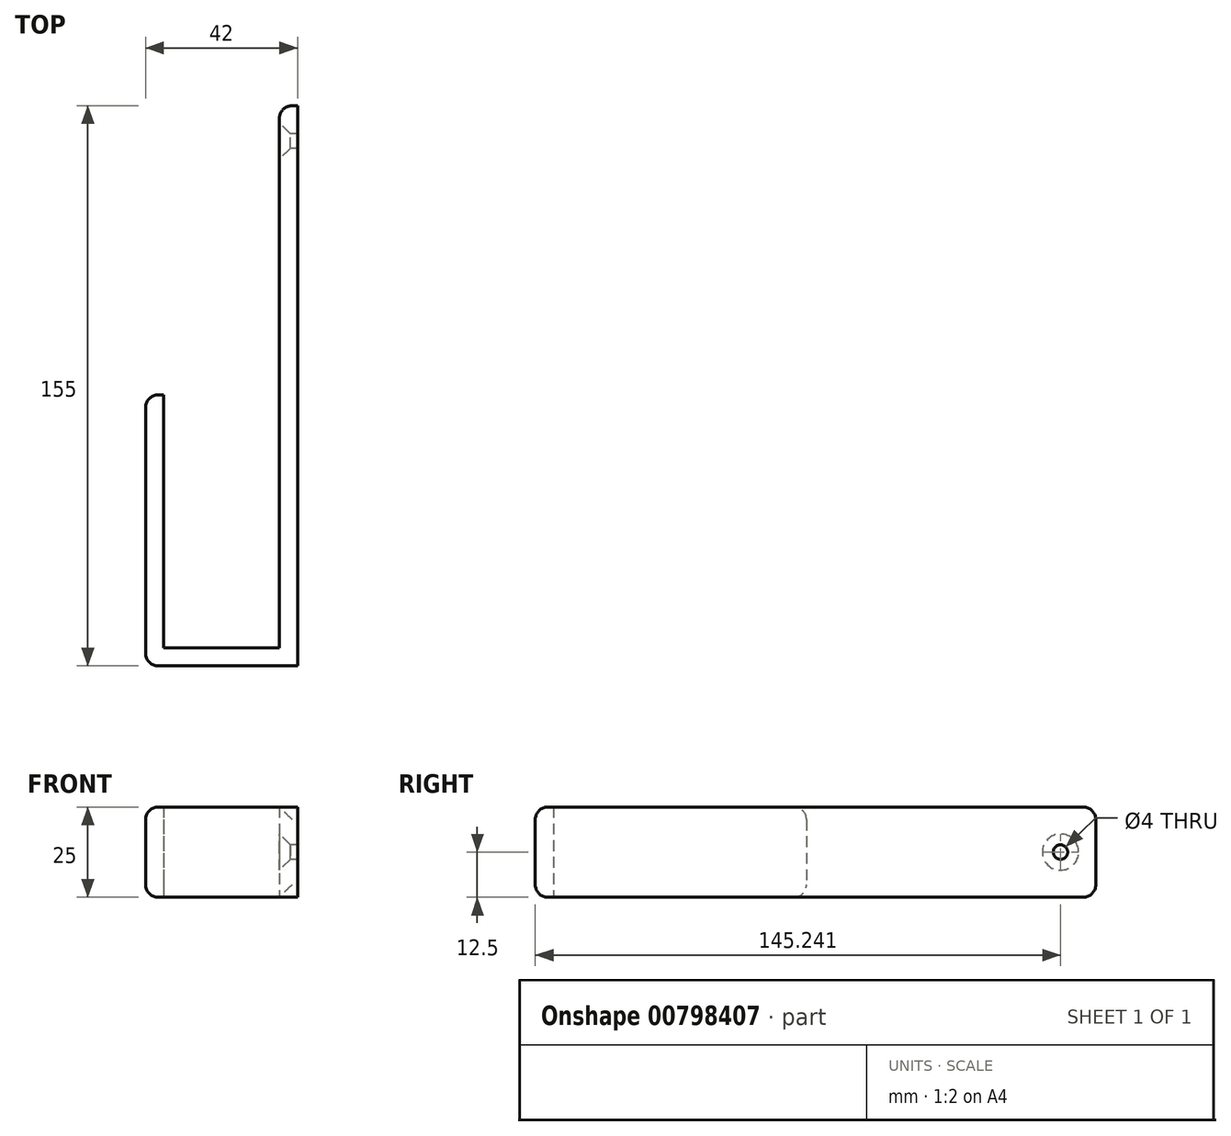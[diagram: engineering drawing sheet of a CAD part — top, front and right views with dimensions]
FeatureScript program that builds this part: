
annotation { "Feature Type Name" : "Feature", "Feature Type Description" : "" }
export const myFeature = defineFeature(function(context is Context, id is Id, definition is map)
    precondition{}
    {
        {
            var Q0;
            Q0=qCreatedBy(makeId("Top.planeOp"),FACE);
            var sketch = newSketch(context, id + "F0", { "sketchPlane" : qUnion([Q0])});
            skLineSegment(sketch, "E0.bottom", {"start": v(-13.63, -47.25) * mm, "end": v(18.37, -47.25) * mm});
            skLineSegment(sketch, "E0.top", {"start": v(-13.63, -42.25) * mm, "end": v(18.37, -42.25) * mm});
            skLineSegment(sketch, "E0.left", {"start": v(-13.63, -47.25) * mm, "end": v(-13.63, -42.25) * mm});
            skLineSegment(sketch, "E0.right", {"start": v(18.37, -47.25) * mm, "end": v(18.37, -42.25) * mm});
            skLineSegment(sketch, "E1.bottom", {"start": v(18.37, -47.25) * mm, "end": v(23.37, -47.25) * mm});
            skLineSegment(sketch, "E1.top", {"start": v(18.37, 107.75) * mm, "end": v(23.37, 107.75) * mm});
            skLineSegment(sketch, "E1.left", {"start": v(18.37, -47.25) * mm, "end": v(18.37, 107.75) * mm});
            skLineSegment(sketch, "E1.right", {"start": v(23.37, -47.25) * mm, "end": v(23.37, 107.75) * mm});
            skLineSegment(sketch, "E2.bottom", {"start": v(-13.63, -47.25) * mm, "end": v(-18.63, -47.25) * mm});
            skLineSegment(sketch, "E2.top", {"start": v(-13.63, 27.75) * mm, "end": v(-18.63, 27.75) * mm});
            skLineSegment(sketch, "E2.left", {"start": v(-13.63, -47.25) * mm, "end": v(-13.63, 27.75) * mm});
            skLineSegment(sketch, "E2.right", {"start": v(-18.63, -47.25) * mm, "end": v(-18.63, 27.75) * mm});
            skSolve(sketch);
        }
        {
            var Q0;
            Q0 = qSketchRegion(id + "F0", true);
            extrude(context, id + "F1", {"entities" : qUnion([Q0]), "depth" : 25 * mm, "offsetDistance" : 25 * mm});
        }
        {
            var Q0;
            Q0=makeQuery(id+"F1.opExtrude","SWEPT_FACE",FACE,{"disambiguationData":[OSD([sQuery(id+"F0.wireOp",EDGE,"E1.left")])]});
            var sketch = newSketch(context, id + "F2", { "sketchPlane" : qUnion([Q0])});
            skCircle(sketch, "E3", {"center": v(-98, 12.5) * mm, "radius": 5 * mm});
            skSolve(sketch);
        }
        {
            var Q0;
            Q0=sQuery(id+"F2.wireOp",VERTEX,"E3.center");
            var Q1;
            Q1=makeQuery(id+"F1.opExtrude","SWEPT_BODY",BODY,{"disambiguationData":[OSD([sQuery(id+"F0.wireOp",EDGE,"E0.bottom"),sQuery(id+"F0.wireOp",EDGE,"E0.top"),sQuery(id+"F0.wireOp",EDGE,"E1.bottom"),sQuery(id+"F0.wireOp",EDGE,"E1.top"),sQuery(id+"F0.wireOp",EDGE,"E1.left"),sQuery(id+"F0.wireOp",EDGE,"E1.right"),sQuery(id+"F0.wireOp",EDGE,"E2.bottom"),sQuery(id+"F0.wireOp",EDGE,"E2.top"),sQuery(id+"F0.wireOp",EDGE,"E2.left"),sQuery(id+"F0.wireOp",EDGE,"E2.right")])]});
            hole(context, id + "F3", {"style" : HoleStyle.C_SINK, "endStyle" : HoleEndStyle.THROUGH, "holeDiameter" : 4 * mm, "cSinkDiameter" : 10 * mm, "cSinkAngle" : 90 * degree, "majorDiameter" : 5 * mm, "isTappedThrough" : true, "tappedDepth" : 12 * mm, "tapClearance" : 3, "locations" : qUnion([Q0]), "scope" : qUnion([Q1])});
        }
        {
            var Q0;
            Q0=makeQuery(id+"F1.opExtrude","CAP_EDGE",EDGE,{"disambiguationData":[OSD([sQuery(id+"F0.wireOp",EDGE,"E2.top")])],"isStart":true});
            var Q1;
            Q1=makeQuery(id+"F1.opExtrude","CAP_EDGE",EDGE,{"disambiguationData":[OSD([sQuery(id+"F0.wireOp",EDGE,"E2.top")])],"isStart":false});
            var Q2;
            Q2=makeQuery(id+"F1.opExtrude","CAP_EDGE",EDGE,{"disambiguationData":[OSD([sQuery(id+"F0.wireOp",EDGE,"E1.top")])],"isStart":true});
            var Q3;
            Q3=makeQuery(id+"F1.opExtrude","CAP_EDGE",EDGE,{"disambiguationData":[OSD([sQuery(id+"F0.wireOp",EDGE,"E1.top")])],"isStart":false});
            var Q4;
            Q4=makeQuery(id+"F1.opExtrude","SWEPT_EDGE",EDGE,{"disambiguationData":[OSD([sQuery(id+"F0.wireOp",EDGE,"E2.top"),sQuery(id+"F0.wireOp",EDGE,"E2.right")])]});
            var Q5;
            Q5=makeQuery(id+"F1.opExtrude","CAP_EDGE",EDGE,{"disambiguationData":[OSD([sQuery(id+"F0.wireOp",EDGE,"E2.right")])],"isStart":false});
            var Q6;
            Q6=makeQuery(id+"F1.opExtrude","CAP_EDGE",EDGE,{"disambiguationData":[OSD([sQuery(id+"F0.wireOp",EDGE,"E2.right")])],"isStart":true});
            var Q7;
            Q7=makeQuery(id+"F1.opExtrude","SWEPT_EDGE",EDGE,{"disambiguationData":[OSD([sQuery(id+"F0.wireOp",EDGE,"E2.bottom"),sQuery(id+"F0.wireOp",EDGE,"E2.right")])]});
            var Q8;
            Q8=makeQuery(id+"F1.opExtrude","CAP_EDGE",EDGE,{"disambiguationData":[OSD([sQuery(id+"F0.wireOp",EDGE,"E0.bottom"),sQuery(id+"F0.wireOp",EDGE,"E1.bottom"),sQuery(id+"F0.wireOp",EDGE,"E2.bottom")])],"isStart":false});
            var Q9;
            Q9=makeQuery(id+"F1.opExtrude","CAP_EDGE",EDGE,{"disambiguationData":[OSD([sQuery(id+"F0.wireOp",EDGE,"E0.bottom"),sQuery(id+"F0.wireOp",EDGE,"E1.bottom"),sQuery(id+"F0.wireOp",EDGE,"E2.bottom")])],"isStart":true});
            var Q10;
            Q10=makeQuery(id+"F1.opExtrude","SWEPT_EDGE",EDGE,{"disambiguationData":[OSD([sQuery(id+"F0.wireOp",EDGE,"E1.top"),sQuery(id+"F0.wireOp",EDGE,"E1.left")])]});
            fillet(context, id + "F4", {"entities" : qUnion([Q0, Q1, Q2, Q3, Q4, Q5, Q6, Q7, Q8, Q9, Q10]), "radius" : 3.5 * mm, "tangentPropagation" : true, "allowEdgeOverflow" : false});
        }
    });
